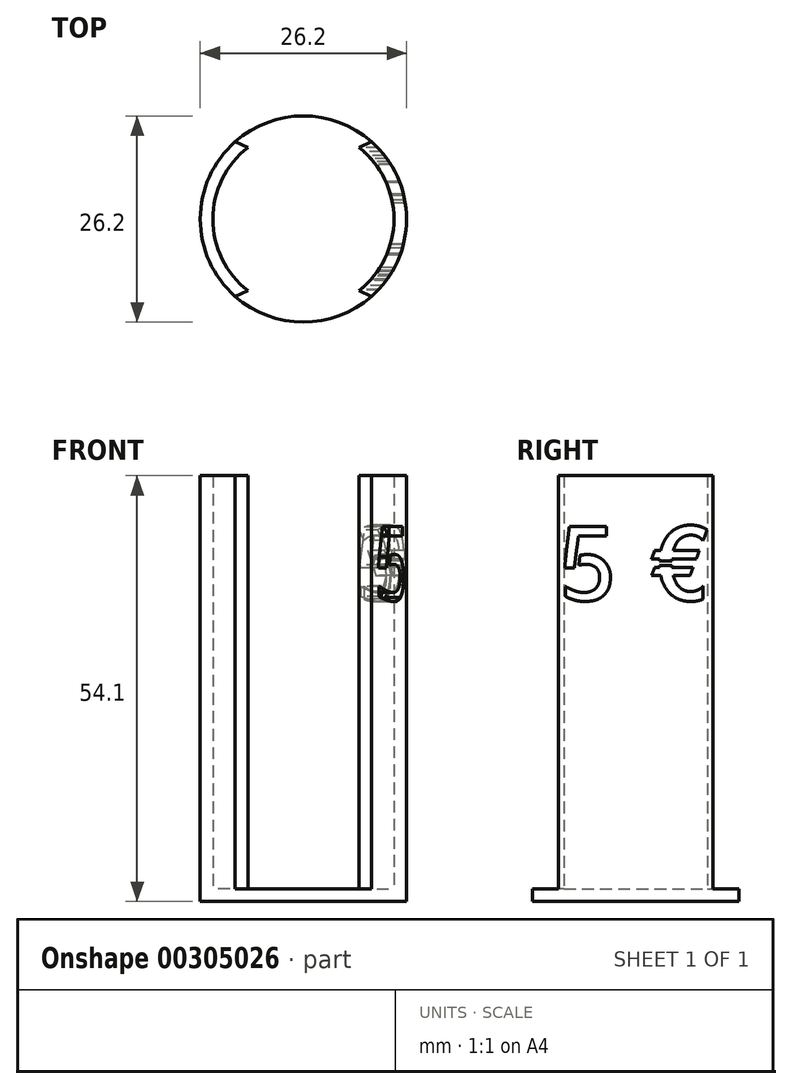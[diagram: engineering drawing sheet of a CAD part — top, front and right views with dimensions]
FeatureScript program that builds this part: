
annotation { "Feature Type Name" : "Feature", "Feature Type Description" : "" }
export const myFeature = defineFeature(function(context is Context, id is Id, definition is map)
    precondition{}
    {
        {
            var Q0;
            Q0=qCreatedBy(makeId("Top.planeOp"),FACE);
            var sketch = newSketch(context, id + "F0", { "sketchPlane" : qUnion([Q0])});
            skCircle(sketch, "E0", {"center": v(0, 0) * mm, "radius": 11.5 * mm});
            skCircle(sketch, "E1.0", {"center": v(0, 0) * mm, "radius": 13.1 * mm});
            skSolve(sketch);
        }
        {
            var Q0;
            Q0=makeQuery(id+"F0.imprint","IMPRINT",FACE,{"disambiguationData":[TD([[makeQuery(id+"F0.imprint","IMPRINT",EDGE,{"derivedFrom":sQuery(id+"F0.wireOp",EDGE,"E0")}),1.0]])]});
            var Q1;
            Q1=makeQuery(id+"F0.imprint","IMPRINT",FACE,{"disambiguationData":[TD([[makeQuery(id+"F0.imprint","IMPRINT",EDGE,{"derivedFrom":sQuery(id+"F0.wireOp",EDGE,"E0")}),-1.0]])]});
            extrude(context, id + "F1", {"entities" : qUnion([Q0, Q1]), "oppositeDirection" : true, "depth" : 1.6 * mm});
        }
        {
            var Q0;
            Q0=makeQuery(id+"F0.imprint","IMPRINT",FACE,{"disambiguationData":[TD([[makeQuery(id+"F0.imprint","IMPRINT",EDGE,{"derivedFrom":sQuery(id+"F0.wireOp",EDGE,"E0")}),-1.0]])]});
            extrude(context, id + "F2", {"entities" : qUnion([Q0]), "operationType" : NewBodyOperationType.ADD, "depth" : 52.5 * mm});
        }
        {
            var Q0;
            Q0=qCreatedBy(makeId("Front.planeOp"),FACE);
            var sketch = newSketch(context, id + "F3", { "sketchPlane" : qUnion([Q0])});
            skLineSegment(sketch, "E2.bottom", {"start": v(-7, 52.5) * mm, "end": v(7, 52.5) * mm});
            skLineSegment(sketch, "E2.top", {"start": v(-7, 0) * mm, "end": v(7, 0) * mm});
            skLineSegment(sketch, "E2.left", {"start": v(-7, 52.5) * mm, "end": v(-7, 0) * mm});
            skLineSegment(sketch, "E2.right", {"start": v(7, 52.5) * mm, "end": v(7, 0) * mm});
            skSolve(sketch);
        }
        {
            var Q0;
            Q0=makeQuery(id+"F3.imprint","IMPRINT",FACE,{"disambiguationData":[TD([[makeQuery(id+"F3.imprint","IMPRINT",EDGE,{"derivedFrom":sQuery(id+"F3.wireOp",EDGE,"E2.bottom")}),-1.0]])]});
            extrude(context, id + "F4", {"entities" : qUnion([Q0]), "operationType" : NewBodyOperationType.REMOVE, "endBound" : BoundingType.THROUGH_ALL, "oppositeDirection" : true, "depth" : 25 * mm, "hasSecondDirection" : true, "secondDirectionBound" : SecondDirectionBoundingType.THROUGH_ALL, "secondDirectionOppositeDirection" : false, "secondDirectionDepth" : 25 * mm});
        }
        {
            var Q0;
            {var subQ0=sQuery(id+"F0.wireOp",EDGE,"E1.0");Q0=makeQuery(id+"F4.boolean.opBoolean","INTERSECT",EDGE,{"disambiguationData":[OD(0.0)],"derivedFrom":[makeQuery(id+"F2.boolean.opBoolean","MERGE",FACE,{"derivedFrom":[makeQuery(id+"F1.opExtrude","SWEPT_FACE",FACE,{"disambiguationData":[OSD([subQ0])]}),makeQuery(id+"F2.opExtrude","SWEPT_FACE",FACE,{"disambiguationData":[OSD([subQ0])]})]}),makeQuery(id+"F4.opExtrude","SWEPT_FACE",FACE,{"disambiguationData":[OSD([sQuery(id+"F3.wireOp",EDGE,"E2.left")])]})]});}
            var Q1;
            {var subQ0=sQuery(id+"F0.wireOp",EDGE,"E1.0");Q1=makeQuery(id+"F4.boolean.opBoolean","INTERSECT",EDGE,{"disambiguationData":[OD(0.0)],"derivedFrom":[makeQuery(id+"F2.boolean.opBoolean","MERGE",FACE,{"derivedFrom":[makeQuery(id+"F1.opExtrude","SWEPT_FACE",FACE,{"disambiguationData":[OSD([subQ0])]}),makeQuery(id+"F2.opExtrude","SWEPT_FACE",FACE,{"disambiguationData":[OSD([subQ0])]})]}),makeQuery(id+"F4.opExtrude","SWEPT_FACE",FACE,{"disambiguationData":[OSD([sQuery(id+"F3.wireOp",EDGE,"E2.right")])]})]});}
            var Q2;
            {var subQ0=sQuery(id+"F0.wireOp",EDGE,"E1.0");Q2=makeQuery(id+"F4.boolean.opBoolean","INTERSECT",EDGE,{"disambiguationData":[OD(1.0)],"derivedFrom":[makeQuery(id+"F2.boolean.opBoolean","MERGE",FACE,{"derivedFrom":[makeQuery(id+"F1.opExtrude","SWEPT_FACE",FACE,{"disambiguationData":[OSD([subQ0])]}),makeQuery(id+"F2.opExtrude","SWEPT_FACE",FACE,{"disambiguationData":[OSD([subQ0])]})]}),makeQuery(id+"F4.opExtrude","SWEPT_FACE",FACE,{"disambiguationData":[OSD([sQuery(id+"F3.wireOp",EDGE,"E2.left")])]})]});}
            var Q3;
            {var subQ0=sQuery(id+"F0.wireOp",EDGE,"E1.0");Q3=makeQuery(id+"F4.boolean.opBoolean","INTERSECT",EDGE,{"disambiguationData":[OD(1.0)],"derivedFrom":[makeQuery(id+"F2.boolean.opBoolean","MERGE",FACE,{"derivedFrom":[makeQuery(id+"F1.opExtrude","SWEPT_FACE",FACE,{"disambiguationData":[OSD([subQ0])]}),makeQuery(id+"F2.opExtrude","SWEPT_FACE",FACE,{"disambiguationData":[OSD([subQ0])]})]}),makeQuery(id+"F4.opExtrude","SWEPT_FACE",FACE,{"disambiguationData":[OSD([sQuery(id+"F3.wireOp",EDGE,"E2.right")])]})]});}
            chamfer(context, id + "F5", {"entities" : qUnion([Q0, Q1, Q2, Q3]), "width" : 1 * mm, "tangentPropagation" : true});
        }
        {
            var Q0;
            Q0=qCreatedBy(makeId("Right.planeOp"),FACE);
            var sketch = newSketch(context, id + "F6", { "sketchPlane" : qUnion([Q0])});
            skText(sketch, "E3", { "text": "5 €", "fontName": "AllertaStencil-Regular.ttf"});
            const initialGuessF6  = {"E3": [-0.01, 0.03658, 1, 0, 0.0095]};
            skSetInitialGuess(sketch, initialGuessF6);
            skSolve(sketch);
        }
        {
            var Q0;
            Q0=qSketchRegion(id+"F6",true);
            extrude(context, id + "F7", {"entities" : qUnion([Q0]), "operationType" : NewBodyOperationType.REMOVE, "depth" : 25 * mm});
        }
    });
